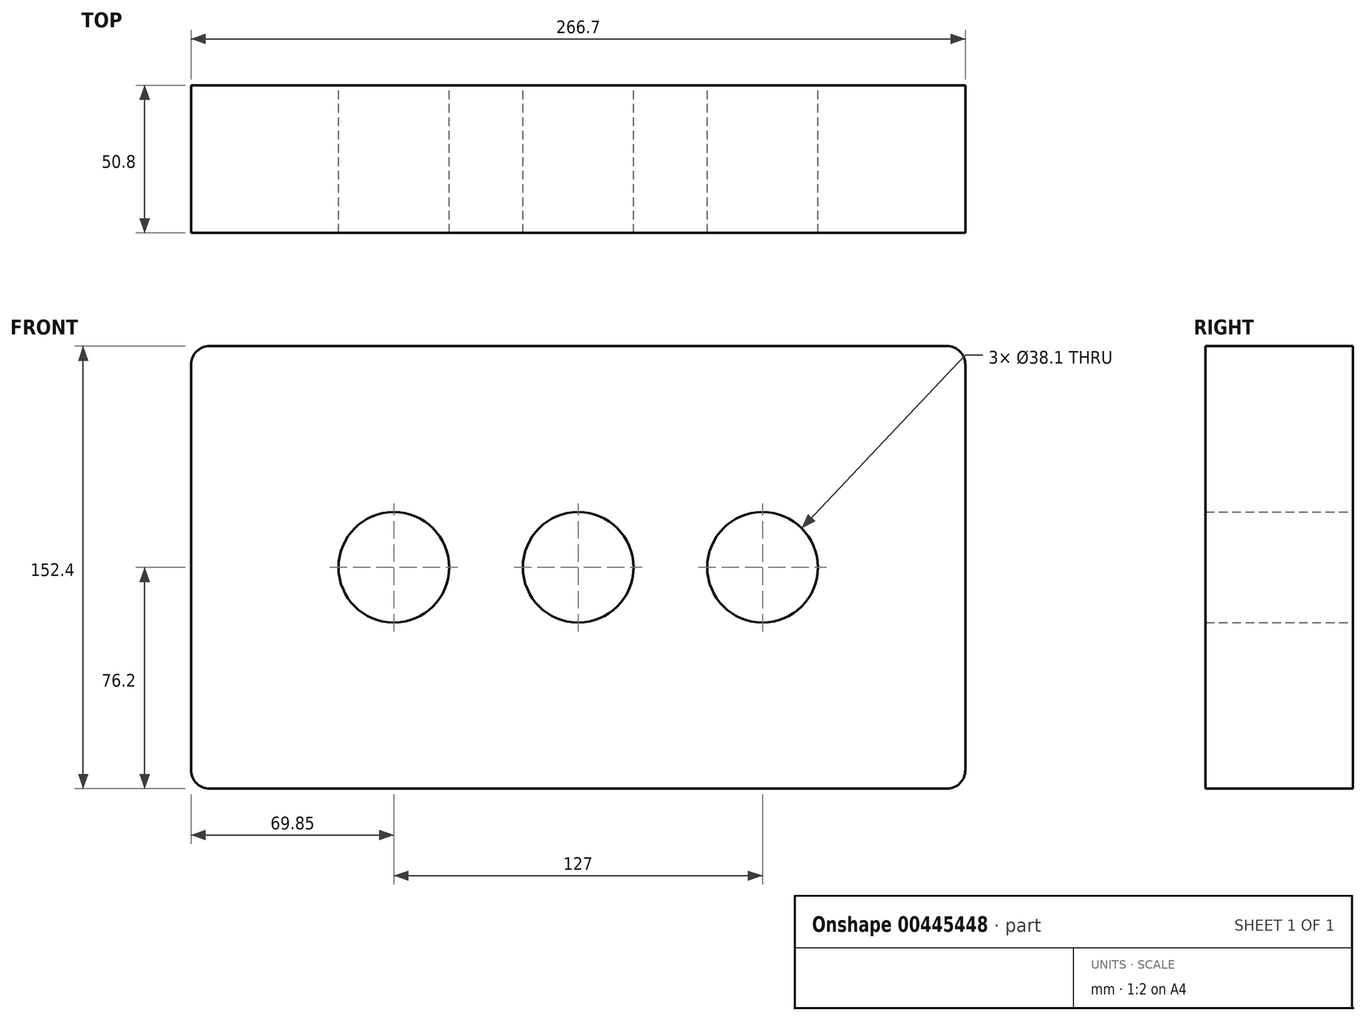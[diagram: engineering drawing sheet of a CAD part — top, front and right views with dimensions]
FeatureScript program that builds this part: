
annotation { "Feature Type Name" : "Feature", "Feature Type Description" : "" }
export const myFeature = defineFeature(function(context is Context, id is Id, definition is map)
    precondition{}
    {
        {
            var Q0;
            Q0=qCreatedBy(makeId("Front.planeOp"),FACE);
            var sketch = newSketch(context, id + "F0", { "sketchPlane" : qUnion([Q0])});
            skLineSegment(sketch, "E0.bottom", {"start": v(127, -76.2) * mm, "end": v(-127, -76.2) * mm});
            skLineSegment(sketch, "E0.top", {"start": v(127, 76.2) * mm, "end": v(-127, 76.2) * mm});
            skLineSegment(sketch, "E0.left", {"start": v(133.35, -69.85) * mm, "end": v(133.35, 69.85) * mm});
            skLineSegment(sketch, "E0.right", {"start": v(-133.35, -69.85) * mm, "end": v(-133.35, 69.85) * mm});
            skPoint(sketch, "E0.middle", {"position": v(0, 0) * mm});
            skCircle(sketch, "E1", {"center": v(0, 0) * mm, "radius": 19.05 * mm});
            skCircle(sketch, "E2", {"center": v(-63.5, 0) * mm, "radius": 19.05 * mm});
            skCircle(sketch, "E3", {"center": v(63.5, 0) * mm, "radius": 19.05 * mm});
            skPoint(sketch, "E4.visualSharp", {"position": v(133.35, 76.2) * mm});
            skArc(sketch, "E4.filletArc", {"start": v(133.35, 69.85) * mm, "mid": v(131.5, 74.34) * mm, "end": v(127, 76.2) * mm});
            skPoint(sketch, "E5.visualSharp", {"position": v(133.35, -76.2) * mm});
            skArc(sketch, "E5.filletArc", {"start": v(127, -76.2) * mm, "mid": v(131.5, -74.34) * mm, "end": v(133.35, -69.85) * mm});
            skPoint(sketch, "E6.visualSharp", {"position": v(-133.35, -76.2) * mm});
            skArc(sketch, "E6.filletArc", {"start": v(-133.35, -69.85) * mm, "mid": v(-131.5, -74.34) * mm, "end": v(-127, -76.2) * mm});
            skPoint(sketch, "E7.visualSharp", {"position": v(-133.35, 76.2) * mm});
            skArc(sketch, "E7.filletArc", {"start": v(-127, 76.2) * mm, "mid": v(-131.5, 74.34) * mm, "end": v(-133.35, 69.85) * mm});
            skSolve(sketch);
        }
        {
            var Q0;
            Q0=makeQuery(id+"F0.imprint","IMPRINT",FACE,{"disambiguationData":[TD([[makeQuery(id+"F0.imprint","IMPRINT",EDGE,{"derivedFrom":sQuery(id+"F0.wireOp",EDGE,"E0.bottom")}),-1.0]])]});
            extrude(context, id + "F1", {"entities" : qUnion([Q0]), "depth" : 50.8 * mm});
        }
        {
            var Q0;
            Q0=makeQuery(id+"F0.imprint","IMPRINT",FACE,{"disambiguationData":[TD([[makeQuery(id+"F0.imprint","IMPRINT",EDGE,{"derivedFrom":sQuery(id+"F0.wireOp",EDGE,"E2")}),1.0]])]});
            var Q1;
            Q1=makeQuery(id+"F0.imprint","IMPRINT",FACE,{"disambiguationData":[TD([[makeQuery(id+"F0.imprint","IMPRINT",EDGE,{"derivedFrom":sQuery(id+"F0.wireOp",EDGE,"E1")}),1.0]])]});
            var Q2;
            Q2=makeQuery(id+"F0.imprint","IMPRINT",FACE,{"disambiguationData":[TD([[makeQuery(id+"F0.imprint","IMPRINT",EDGE,{"derivedFrom":sQuery(id+"F0.wireOp",EDGE,"E3")}),1.0]])]});
            extrude(context, id + "F2", {"entities" : qUnion([Q0, Q1, Q2]), "operationType" : NewBodyOperationType.REMOVE, "oppositeDirection" : true, "depth" : 25.4 * mm});
        }
    });
